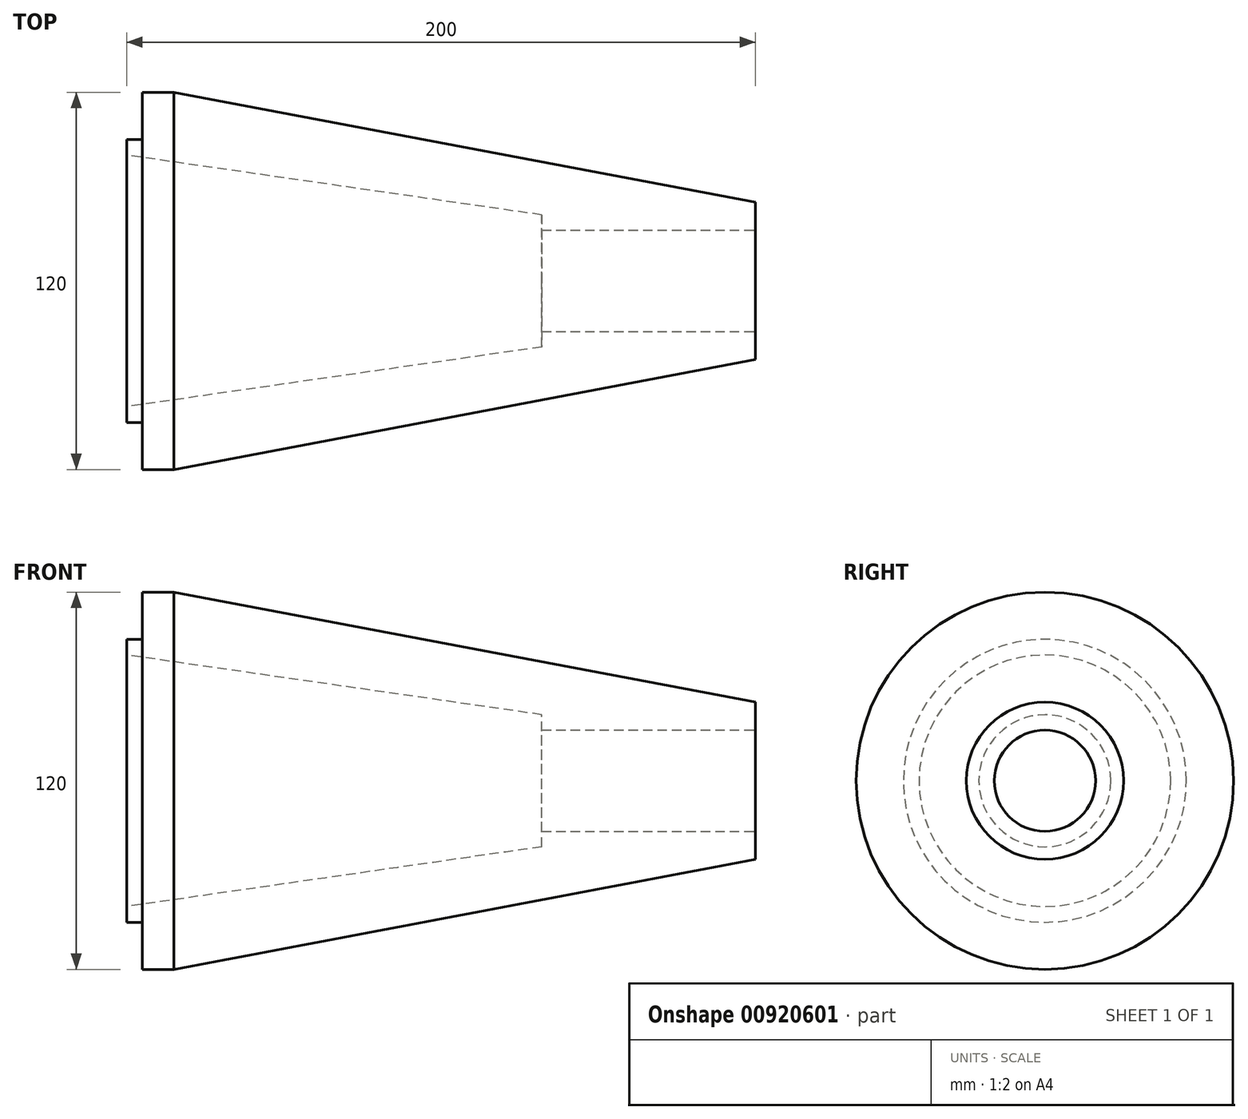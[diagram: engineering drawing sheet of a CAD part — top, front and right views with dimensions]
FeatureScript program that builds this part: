
annotation { "Feature Type Name" : "Feature", "Feature Type Description" : "" }
export const myFeature = defineFeature(function(context is Context, id is Id, definition is map)
    precondition{}
    {
        {
            var Q0;
            Q0=qCreatedBy(makeId("Front.planeOp"),FACE);
            var sketch = newSketch(context, id + "F0", { "sketchPlane" : qUnion([Q0])});
            skLineSegment(sketch, "E0", {"start": v(0, 0) * mm, "end": v(-86.96, 0) * mm, "construction": true});
            skLineSegment(sketch, "E1", {"start": v(5, 60) * mm, "end": v(15, 60) * mm});
            skLineSegment(sketch, "E2", {"start": v(200, 25) * mm, "end": v(200, 16.1) * mm});
            skLineSegment(sketch, "E3", {"start": v(200, 16.1) * mm, "end": v(132, 16.1) * mm});
            skLineSegment(sketch, "E4", {"start": v(132, 16.1) * mm, "end": v(132, 21) * mm});
            skLineSegment(sketch, "E5", {"start": v(0, 40) * mm, "end": v(0, 45) * mm});
            skLineSegment(sketch, "E6", {"start": v(0, 45) * mm, "end": v(5, 45) * mm});
            skLineSegment(sketch, "E7", {"start": v(5, 45) * mm, "end": v(5, 60) * mm});
            skPoint(sketch, "E8.orphan", {"position": v(0, 60) * mm});
            skLineSegment(sketch, "E9", {"start": v(132, 21) * mm, "end": v(0, 40) * mm});
            skLineSegment(sketch, "E10", {"start": v(15, 60) * mm, "end": v(200, 25) * mm});
            skSolve(sketch);
        }
        {
            var Q0;
            Q0=makeQuery(id+"F0.imprint","IMPRINT",FACE,{"disambiguationData":[TD([[makeQuery(id+"F0.imprint","IMPRINT",EDGE,{"derivedFrom":sQuery(id+"F0.wireOp",EDGE,"E1")}),-1.0]])]});
            var Q1;
            Q1=sQuery(id+"F0.wireOp",EDGE,"E0");
            revolve(context, id + "F1", {"surfaceOperationType" : NewSurfaceOperationType.NEW, "entities" : qUnion([Q0]), "axis" : qUnion([Q1]), "revolveType" : RevolveType.FULL});
        }
    });
